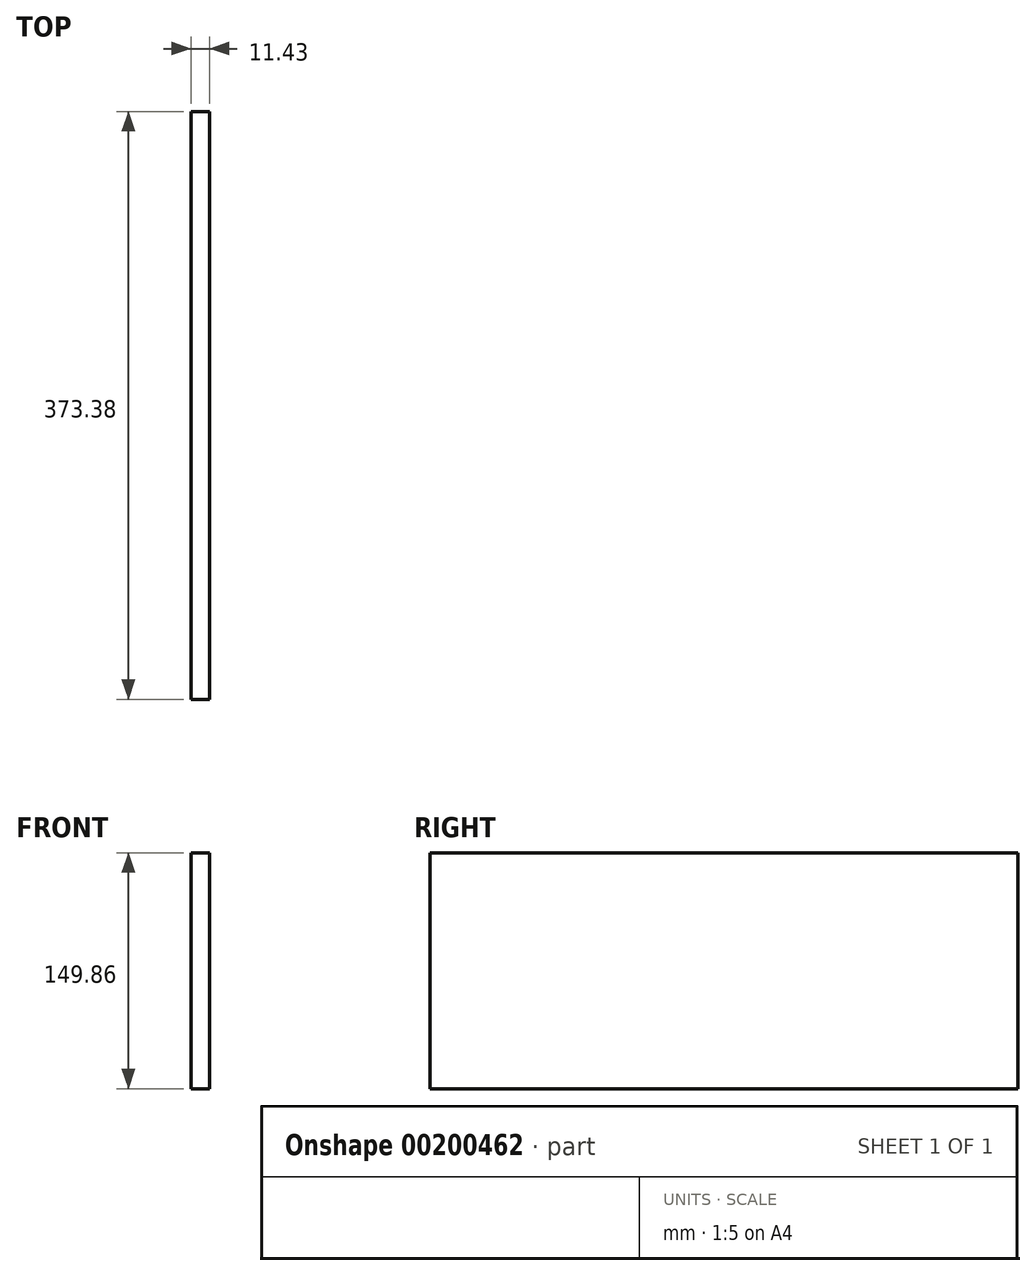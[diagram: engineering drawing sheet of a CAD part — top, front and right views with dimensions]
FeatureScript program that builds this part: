
annotation { "Feature Type Name" : "Feature", "Feature Type Description" : "" }
export const myFeature = defineFeature(function(context is Context, id is Id, definition is map)
    precondition{}
    {
        {
            var Q0;
            Q0=qCreatedBy(makeId("Right.planeOp"),FACE);
            var sketch = newSketch(context, id + "F0", { "sketchPlane" : qUnion([Q0])});
            skLineSegment(sketch, "E0.bottom", {"start": v(-1056.33, -28.37) * mm, "end": v(-682.95, -28.37) * mm});
            skLineSegment(sketch, "E0.top", {"start": v(-1056.33, -178.23) * mm, "end": v(-682.95, -178.23) * mm});
            skLineSegment(sketch, "E0.left", {"start": v(-1056.33, -28.37) * mm, "end": v(-1056.33, -178.23) * mm});
            skLineSegment(sketch, "E0.right", {"start": v(-682.95, -28.37) * mm, "end": v(-682.95, -178.23) * mm});
            skSolve(sketch);
        }
        {
            var Q0;
            Q0 = qSketchRegion(id + "F0", true);
            extrude(context, id + "F1", {"entities" : qUnion([Q0]), "depth" : 11.43 * mm});
        }
    });
